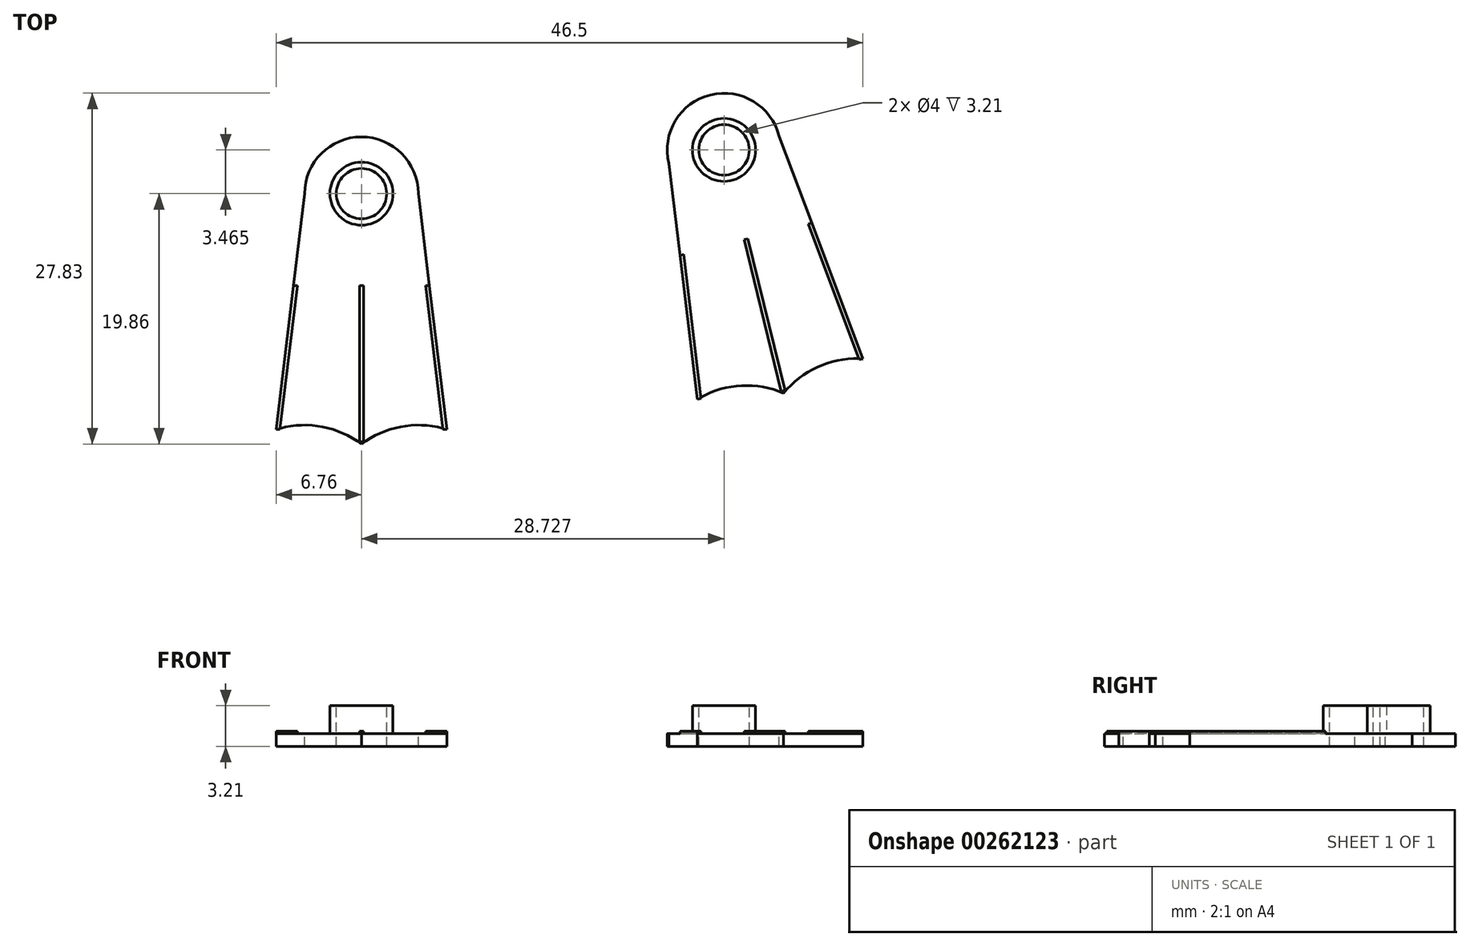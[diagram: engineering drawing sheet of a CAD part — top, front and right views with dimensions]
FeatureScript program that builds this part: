
annotation { "Feature Type Name" : "Feature", "Feature Type Description" : "" }
export const myFeature = defineFeature(function(context is Context, id is Id, definition is map)
    precondition{}
    {
        {
            var Q0;
            Q0=qCreatedBy(makeId("Top.planeOp"),FACE);
            var sketch = newSketch(context, id + "F0", { "sketchPlane" : qUnion([Q0])});
            skCircle(sketch, "E0", {"center": v(0, 0) * mm, "radius": 2.5 * mm});
            skSolve(sketch);
        }
        {
            var Q0;
            Q0=makeQuery(id+"F0.imprint","IMPRINT",FACE,{"disambiguationData":[TD([[makeQuery(id+"F0.imprint","IMPRINT",EDGE,{"derivedFrom":sQuery(id+"F0.wireOp",EDGE,"E0")}),1.0]])]});
            extrude(context, id + "F1", {"entities" : qUnion([Q0]), "depth" : 2.2 * mm});
        }
        {
            var Q0;
            Q0=makeQuery(id+"F1.opExtrude","CAP_FACE",FACE,{"disambiguationData":[OSD([sQuery(id+"F0.wireOp",EDGE,"E0")])],"isStart":true});
            var sketch = newSketch(context, id + "F2", { "sketchPlane" : qUnion([Q0])});
            skCircle(sketch, "E1", {"center": v(0, 0) * mm, "radius": 4.5 * mm});
            skLineSegment(sketch, "E2", {"start": v(-4.5, 0) * mm, "end": v(-6.9, 19.86) * mm});
            skLineSegment(sketch, "E3", {"start": v(4.5, 0) * mm, "end": v(6.9, 19.86) * mm});
            skLineSegment(sketch, "E4", {"start": v(-6.9, 19.86) * mm, "end": v(6.9, 19.86) * mm});
            skLineSegment(sketch, "E5", {"start": v(0, 0) * mm, "end": v(0, 19.86) * mm, "construction": true});
            skSolve(sketch);
        }
        {
            var Q0;
            Q0 = qSketchRegion(id + "F2", true);
            extrude(context, id + "F3", {"entities" : qUnion([Q0]), "operationType" : NewBodyOperationType.ADD, "depth" : 1 * mm});
        }
        {
            var Q0;
            Q0=makeQuery(id+"F1.opExtrude","CAP_FACE",FACE,{"disambiguationData":[OSD([sQuery(id+"F0.wireOp",EDGE,"E0")])],"isStart":false});
            var sketch = newSketch(context, id + "F4", { "sketchPlane" : qUnion([Q0])});
            skCircle(sketch, "E6", {"center": v(0, 0) * mm, "radius": 2 * mm});
            skSolve(sketch);
        }
        {
            var Q0;
            Q0=makeQuery(id+"F4.imprint","IMPRINT",FACE,{"disambiguationData":[TD([[makeQuery(id+"F4.imprint","IMPRINT",EDGE,{"derivedFrom":sQuery(id+"F4.wireOp",EDGE,"E6")}),1.0]])]});
            extrude(context, id + "F5", {"entities" : qUnion([Q0]), "operationType" : NewBodyOperationType.REMOVE, "oppositeDirection" : true, "depth" : 25 * mm});
        }
        {
            var Q0;
            {var subQ0=sQuery(id+"F2.wireOp",EDGE,"E2");Q0=makeQuery(id+"F2.imprint","IMPRINT",FACE,{"disambiguationData":[TD([[makeQuery(id+"F2.imprint","IMPRINT",EDGE,{"derivedFrom":subQ0}),-1.0]])]});}
            var sketch = newSketch(context, id + "F6", { "sketchPlane" : qUnion([Q0])});
            skCircle(sketch, "E7", {"center": v(-4.5, 25.85) * mm, "radius": 7.5 * mm});
            skCircle(sketch, "E8", {"center": v(4.5, 25.85) * mm, "radius": 7.5 * mm});
            skSolve(sketch);
        }
        {
            var Q0;
            Q0 = qSketchRegion(id + "F6", true);
            extrude(context, id + "F7", {"entities" : qUnion([Q0]), "operationType" : NewBodyOperationType.REMOVE, "depth" : 25 * mm});
        }
        {
            var Q0;
            {var subQ0=sQuery(id+"F2.wireOp",EDGE,"E2");Q0=makeQuery(id+"F2.imprint","IMPRINT",FACE,{"disambiguationData":[TD([[makeQuery(id+"F2.imprint","IMPRINT",EDGE,{"derivedFrom":subQ0}),-1.0]])]});}
            var sketch = newSketch(context, id + "F8", { "sketchPlane" : qUnion([Q0])});
            skLineSegment(sketch, "E9", {"start": v(-5.38, 7.3) * mm, "end": v(-6.76, 18.7) * mm});
            skLineSegment(sketch, "E10", {"start": v(-5.38, 7.3) * mm, "end": v(5.08, 7.3) * mm, "construction": true});
            skLineSegment(sketch, "E11", {"start": v(-6.76, 18.7) * mm, "end": v(-6.46, 18.7) * mm});
            skLineSegment(sketch, "E12", {"start": v(-6.46, 18.7) * mm, "end": v(-5.08, 7.3) * mm});
            skLineSegment(sketch, "E13", {"start": v(-5.08, 7.3) * mm, "end": v(-5.38, 7.3) * mm});
            skLineSegment(sketch, "E14", {"start": v(5.38, 7.3) * mm, "end": v(6.76, 18.7) * mm});
            skLineSegment(sketch, "E15", {"start": v(5.38, 7.3) * mm, "end": v(5.08, 7.3) * mm});
            skLineSegment(sketch, "E16", {"start": v(5.08, 7.3) * mm, "end": v(6.46, 18.7) * mm});
            skLineSegment(sketch, "E17", {"start": v(6.46, 18.7) * mm, "end": v(6.76, 18.7) * mm});
            skLineSegment(sketch, "E18", {"start": v(0, 7.3) * mm, "end": v(0, 24.68) * mm, "construction": true});
            skLineSegment(sketch, "E19", {"start": v(-0.15, 7.3) * mm, "end": v(-0.15, 19.67) * mm});
            skLineSegment(sketch, "E20", {"start": v(-0.15, 19.67) * mm, "end": v(0.15, 19.67) * mm});
            skLineSegment(sketch, "E21", {"start": v(0.15, 19.67) * mm, "end": v(0.15, 7.3) * mm});
            skLineSegment(sketch, "E22", {"start": v(0.15, 7.3) * mm, "end": v(-0.15, 7.3) * mm});
            skSolve(sketch);
        }
        {
            var Q0;
            Q0 = qSketchRegion(id + "F8", true);
            extrude(context, id + "F9", {"entities" : qUnion([Q0]), "operationType" : NewBodyOperationType.ADD, "oppositeDirection" : true, "depth" : .2 * mm});
        }
        {
            var Q0;
            Q0=makeQuery(id+"F9.boolean.opBoolean","MERGE",FACE,{"derivedFrom":[makeQuery(id+"F3.opExtrude","SWEPT_FACE",FACE,{"disambiguationData":[OSD([sQuery(id+"F2.wireOp",EDGE,"E3")])]}),makeQuery(id+"F9.opExtrude","SWEPT_FACE",FACE,{"disambiguationData":[OSD([sQuery(id+"F8.wireOp",EDGE,"E14")])]})]});
            cPlane(context, id + "F10", {"entities" : qUnion([Q0]), "cplaneType" : CPlaneType.OFFSET, "offset" : 10 * mm, "width" : 150 * mm, "height" : 150 * mm});
        }
        {
            var Q0;
            Q0=makeQuery(id+"F1.opExtrude","SWEPT_BODY",BODY,{"disambiguationData":[OSD([sQuery(id+"F0.wireOp",EDGE,"E0")])]});
            var Q1;
            Q1=qCreatedBy(id+"F10.planeOp",FACE);
            mirror(context, id + "F11", {"entities" : qUnion([Q0]), "mirrorPlane" : qUnion([Q1])});
        }
    });
